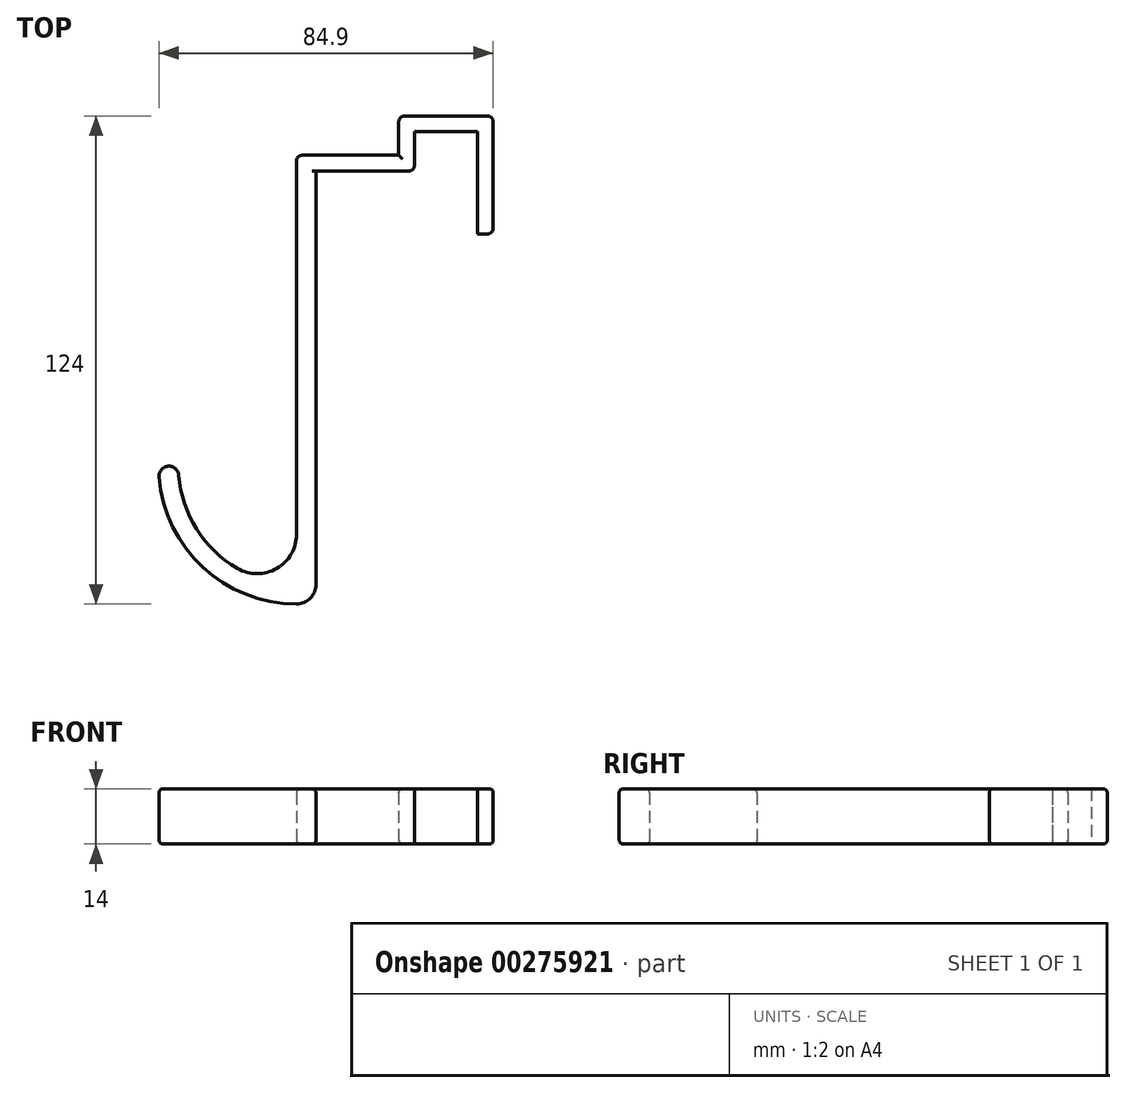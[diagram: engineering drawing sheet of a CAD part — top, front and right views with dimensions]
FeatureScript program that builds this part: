
annotation { "Feature Type Name" : "Feature", "Feature Type Description" : "" }
export const myFeature = defineFeature(function(context is Context, id is Id, definition is map)
    precondition{}
    {
        {
            var Q0;
            Q0=qCreatedBy(makeId("Top.planeOp"),FACE);
            var sketch = newSketch(context, id + "F0", { "sketchPlane" : qUnion([Q0])});
            skLineSegment(sketch, "E0", {"start": v(45, -14.5) * mm, "end": v(45, 12.5) * mm});
            skLineSegment(sketch, "E1", {"start": v(43.5, 14) * mm, "end": v(22.5, 14) * mm});
            skLineSegment(sketch, "E2", {"start": v(21, 12.5) * mm, "end": v(21, 4) * mm});
            skLineSegment(sketch, "E3", {"start": v(21, 4) * mm, "end": v(-3.5, 4) * mm});
            skLineSegment(sketch, "E4", {"start": v(-5, 2.5) * mm, "end": v(-5, -92.32) * mm});
            skLineSegment(sketch, "E5", {"start": v(-37.4, -75) * mm, "end": v(-37.4, -75) * mm});
            skLineSegment(sketch, "E6", {"start": v(-5, -110) * mm, "end": v(-5, -110) * mm});
            skLineSegment(sketch, "E7", {"start": v(0, 0) * mm, "end": v(23.5, 0) * mm});
            skLineSegment(sketch, "E8", {"start": v(25, 1.5) * mm, "end": v(25, 10) * mm});
            skLineSegment(sketch, "E9", {"start": v(25, 10) * mm, "end": v(41, 10) * mm});
            skLineSegment(sketch, "E10", {"start": v(41, 10) * mm, "end": v(41, -16) * mm});
            skLineSegment(sketch, "E11", {"start": v(41, -16) * mm, "end": v(43.5, -16) * mm});
            skLineSegment(sketch, "E12.trimOffspring", {"start": v(0, -105) * mm, "end": v(0, 0) * mm});
            skArc(sketch, "E13", {"start": v(-34.91, -77.3) * mm, "mid": v(-30.38, -90.99) * mm, "end": v(-20, -100.98) * mm});
            skArc(sketch, "E14", {"start": v(-39.9, -77.7) * mm, "mid": v(-28.78, -100.68) * mm, "end": v(-5, -110) * mm});
            skPoint(sketch, "E15.visualSharp", {"position": v(-35, -75) * mm});
            skArc(sketch, "E15.filletArc", {"start": v(-34.91, -77.3) * mm, "mid": v(-35.7, -75.67) * mm, "end": v(-37.4, -75) * mm});
            skPoint(sketch, "E16.visualSharp", {"position": v(-40, -75) * mm});
            skArc(sketch, "E16.filletArc", {"start": v(-37.4, -75) * mm, "mid": v(-39.24, -75.8) * mm, "end": v(-39.9, -77.7) * mm});
            skPoint(sketch, "E17.visualSharp", {"position": v(-5, 4) * mm});
            skArc(sketch, "E17.filletArc", {"start": v(-3.5, 4) * mm, "mid": v(-4.56, 3.56) * mm, "end": v(-5, 2.5) * mm});
            skPoint(sketch, "E18.visualSharp", {"position": v(25, 0) * mm});
            skArc(sketch, "E18.filletArc", {"start": v(23.5, 0) * mm, "mid": v(24.56, 0.44) * mm, "end": v(25, 1.5) * mm});
            skPoint(sketch, "E19.visualSharp", {"position": v(21, 14) * mm});
            skArc(sketch, "E19.filletArc", {"start": v(22.5, 14) * mm, "mid": v(21.44, 13.56) * mm, "end": v(21, 12.5) * mm});
            skPoint(sketch, "E20.visualSharp", {"position": v(45, 14) * mm});
            skArc(sketch, "E20.filletArc", {"start": v(45, 12.5) * mm, "mid": v(44.56, 13.56) * mm, "end": v(43.5, 14) * mm});
            skPoint(sketch, "E21.visualSharp", {"position": v(45, -16) * mm});
            skArc(sketch, "E21.filletArc", {"start": v(43.5, -16) * mm, "mid": v(44.56, -15.56) * mm, "end": v(45, -14.5) * mm});
            skArc(sketch, "E22", {"start": v(-20, -100.98) * mm, "mid": v(-10, -100.98) * mm, "end": v(-5, -92.32) * mm});
            skPoint(sketch, "E23.orphan", {"position": v(-5, -105) * mm});
            skPoint(sketch, "E24.visualSharp", {"position": v(0, -110) * mm});
            skArc(sketch, "E24.filletArc", {"start": v(-5, -110) * mm, "mid": v(-1.46, -108.54) * mm, "end": v(0, -105) * mm});
            skSolve(sketch);
        }
        {
            var Q0;
            Q0=qSketchRegion(id+"F0",true);
            extrude(context, id + "F1", {"entities" : qUnion([Q0]), "depth" : 14 * mm});
        }
        {
            var Q0;
            Q0=makeQuery(id+"F1.opExtrude","CAP_EDGE",EDGE,{"disambiguationData":[OSD([sQuery(id+"F0.wireOp",EDGE,"E0")])],"isStart":false});
            var Q1;
            Q1=makeQuery(id+"F1.opExtrude","CAP_EDGE",EDGE,{"disambiguationData":[OSD([sQuery(id+"F0.wireOp",EDGE,"E20.filletArc")])],"isStart":false});
            var Q2;
            Q2=makeQuery(id+"F1.opExtrude","CAP_EDGE",EDGE,{"disambiguationData":[OSD([sQuery(id+"F0.wireOp",EDGE,"E1")])],"isStart":false});
            var Q3;
            Q3=makeQuery(id+"F1.opExtrude","CAP_EDGE",EDGE,{"disambiguationData":[OSD([sQuery(id+"F0.wireOp",EDGE,"E3")])],"isStart":false});
            var Q4;
            Q4=makeQuery(id+"F1.opExtrude","CAP_EDGE",EDGE,{"disambiguationData":[OSD([sQuery(id+"F0.wireOp",EDGE,"E4")])],"isStart":true});
            var Q5;
            Q5=makeQuery(id+"F1.opExtrude","CAP_EDGE",EDGE,{"disambiguationData":[OSD([sQuery(id+"F0.wireOp",EDGE,"E2")])],"isStart":true});
            fillet(context, id + "F2", {"entities" : qUnion([Q0, Q1, Q2, Q3, Q4, Q5]), "radius" : 1 * mm, "tangentPropagation" : true, "allowEdgeOverflow" : false});
        }
    });
